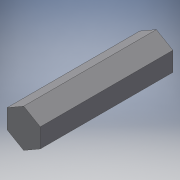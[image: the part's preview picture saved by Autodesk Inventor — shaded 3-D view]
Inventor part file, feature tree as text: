
AUTODESK INVENTOR PART (.ipt)
format: ipt  version: 2018 (Build 220112000, 112)  size: 92,160 bytes
history: native  units: in
note: dims shown in document units (in); Inventor stores cm internally (conversion verified against a paired STEP export)
features: extrude x1, sketch x1
ambient origin geometry x8: Origin, YZ Plane, XZ Plane, XY Plane, X Axis, Y Axis, Z Axis, Center Point
bodies: Solid1 (feature_tree)
feature tree (2):
  extrude  "Extrusion1"  Depth=2.0in TaperAngle=0.0deg
  sketch  "Sketch1"  dims[d0=0.5in d1=2.0in d2=0.0in]
